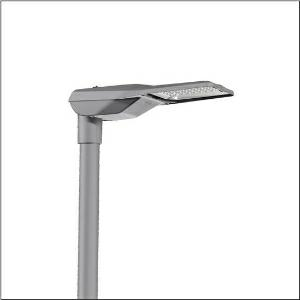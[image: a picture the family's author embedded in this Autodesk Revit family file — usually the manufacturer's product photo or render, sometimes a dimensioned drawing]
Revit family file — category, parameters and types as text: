
# Revit family: streetlight_sl_21_iq_mini___st1_0a_5xe2d31v08gb_747e
name_source: partatom
category: Lighting Fixtures
units: mm (PartAtom-declared; Revit-internal decimal feet)

## family parameters
Cut with Voids When Loaded = No
Host = Face
Light Source = No
Part Type = Normal
Room Calculation Point = No
Round Connector Dimension = Use Diameter
Shared = No

## types (1)
- --- (1 x LED, 5990 lm, 39.8 W, 3000K)
    Apparent Load = 40 VA
    CIE Flux Codes = 37 72 97 100 100
    Color Rendering = 70
    Color Temperature = 3000K
    Default Elevation = 1800 mm
    Description = Streetlight SL 21 iQ mini, mast luminaire, primary light control with lens, of PMMA, primary optical cover: cover, of toughened safety glass, transparent, light distribution: ST1.0a, light emission: direct distribution, primary light characteristic: asymmetric, installation type: post-top, side-entry, LED, High Power LED, rated luminous flux: 5.990lm, luminous efficacy: 151lm/W, light colour: 730, colour temperature: 3000K, control gear: iQ-Street Remote, D4i with power reduction, control: pre-setting: logarithmic dimming characteristic, Street-Remote, Auto-Match, Temp-Guard, Lumen-Switch, Night-Set, Smart-Wire, Light-Fading, Desk-Remote (wireless, voltage-free reading and setting of iQ features in the workshop via application-optimized NFC function/RFID function), optimised constant luminous flux control (CLO 2.0), mains connection: 220..240V, AC, 50/60Hz, start of lifetime: 40W, end of service life: 41W, reduction: 18W, luminaire housing, of diecast aluminium, powder-coated, Siteco® metallic grey (DB 702S), corrosivity category C5 mid according to DIN EN ISO 12944, please order mast flange separately, inclination adjustable: 0°, 5°, 10°, 15°, sealing non-destructively replaceable, multi-level sealing system, length: 628mm, width: 235mm, height: 110mm, mast flange for spigot size: 42mm (side-entry): 5XC10008XM4, 60/48mm (side-entry/post-top): 5XC10108XM2, 76/60mm (side-entry/post-top): 5XC10108XM1, mounting height: 4..8m, Smart Interface above, protection rating (complete): IP66, insulation class (complete): insulation class II (safety insulation), certification: CE, ENEC, ENEC+, VDE, impact resistance: IK10, permissible operating ambient temperature for outdoor applications: -40..+50°C, standard-compliant lighting for roads and squares, packaging unit: 1 piece

Light Distribution: ST1.0a
    Height = 110 mm
    Lamp = 1 x LED
    Lamp Light Flux = 5990 lm
    Lamp Power = 39.8 W
    Lamp count = 1
    Length = 625 mm
    Luminous efficacy = 151 lm/W
    Manufacturer = Siteco
    ModVariant = No
    Model = 5XE2D31V08GB
    Number of Poles = 1
    OnlyDefault = Yes
    Power Factor = 1
    Product Name = Streetlight SL 21 iQ mini | ST1.0a
    Product group = mast luminaire | pylon top
    ProductGroupID = 6100
    Protection Class = Protection class II
    Protection Degree = IP 66
    RLX_Detail_Level = 1
    RLX_Emergency_Light_Flux = 0 lm
    RLX_Emergency_Type = 0
    RLX_Emergency_Type_DB = No
    RlxData = <blob elided: 92765 chars, md5=0c807cdc>
    Socket = socket
    Standby Power = 0 W
    System Light Flux = 5990 lm
    System Power = 40 W
    Type Comments = factory setting: luminous flux: 100 % | dim-lin: 254 | 800 mA
    Type Image = l_1003515.jpg
    URL = http://relux.com
    VarID = @adj_136625
    Voltage = 0 V
    Weight = 0.00 kg
    Width = 234 mm

## geometry (parser evidence)
native form markers: Blend x4, Sweep x11
no freeform markers — native parametric forms only
